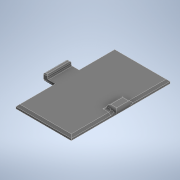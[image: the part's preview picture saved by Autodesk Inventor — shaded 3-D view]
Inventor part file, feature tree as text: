
AUTODESK INVENTOR PART (.ipt)
format: ipt  version: 2022 (Build 260153000, 153)  size: 173,568 bytes
history: native  units: mm
features: extrude x4, sketch x4, fillet x3, chamfer x1
ambient origin geometry x8: Origin, YZ Plane, XZ Plane, XY Plane, X Axis, Y Axis, Z Axis, Center Point
bodies: Solid1 (feature_tree)
feature tree (12):
  extrude  "Extrusion1"  Depth=50.0mm
  extrude  "Extrusion2"  Depth=4.0mm
  fillet  "Fillet1"  Radius=8.0mm
  extrude  "Extrusion3"  Depth=3.0mm
  extrude  "Extrusion4"  Depth=1.0mm
  fillet  "Fillet2"  Radius=6.0mm
  fillet  "Fillet3"  Radius=12.0mm
  chamfer  "Chamfer1"  Distance=5.0mm
  sketch  "Sketch1"  dims[d0=50.0mm d1=28.0mm]
  sketch  "Sketch2"  dims[d2=2.0mm d3=0.0mm d4=4.0mm d5=8.0mm]
  sketch  "Sketch3"  dims[d6=2.0mm d7=3.0mm]
  sketch  "Sketch4"  dims[d8=2.0mm d9=0.0mm d10=1.0mm d11=6.0mm d12=12.0mm d13=5.0mm d14=0.0mm d15=2.0mm d16=1.8mm d17=0.0mm d18=0.5mm d19=1.0mm d20=1.0mm d21=2.0mm d22=45.0deg]
